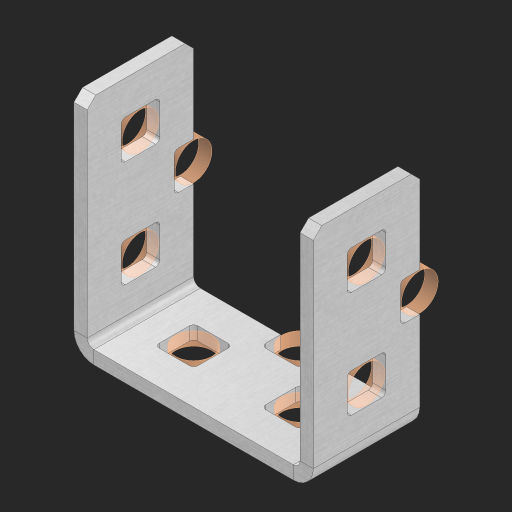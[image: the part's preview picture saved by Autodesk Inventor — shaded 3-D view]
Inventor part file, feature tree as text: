
AUTODESK INVENTOR PART (.ipt)
format: ipt  version: 2023 (Build 270158000, 158)  size: 576,512 bytes
history: native  units: in
note: dims shown in document units (in); Inventor stores cm internally (conversion verified against a paired STEP export)
features: other x90, extrude x82, sheet_metal_op x8, sketch x7, mirror x3, pattern_linear x2, chamfer x1
ambient origin geometry x8: Origin, YZ Plane, XZ Plane, XY Plane, X Axis, Y Axis, Z Axis, Center Point
bodies: Solid1 (feature_tree), Body (feature_tree)
feature tree (193):
  sheet_metal_op  "Flanges"
  sheet_metal_op  "Body Pattern"
  pattern_linear  "Center Pattern"  Spacing1=1.0in  [1 undecoded]
  other  "Arc Length"
  mirror  "Notch Mirror"
  pattern_linear  "Notch Pattern"  Spacing1=0.25in  [1 undecoded]
  other  "Diagonal Plane"
  mirror  "Flange 1"
  mirror  "Flange 2"
  chamfer  "End Chamfer"
  sketch  "Sketch1"  dims[d0=1.0in]
  other  "Plate1"
  sketch  "Sketch2"  dims[d1=0.5in]
  other  "Plate2"
  sheet_metal_op  "Bend1"
  sheet_metal_op  "Corner1"
  sketch  "Sketch8"  dims[d2=0.0625in]
  sketch  "Sketch9"  dims[d3=0.0625in]
  other  "Srf91"
  sheet_metal_op  "Body Pattern Sketch"
  other  "Srf92"
  sketch  "Sketch13"  dims[d4=0.0312in]
  sketch  "Sketch15"  dims[d5=0.125in]
  sketch  "Sketch16"  dims[d6=0.0625in d7=1.0in d8=90.0deg d9=0.0312in d10=0.25in d11=0.0625in d12=0.0625in d49=0.182in d50=0.02in d52=0.25in d53=0.0625in d54=0.0in d55=0.172in d56=1.0in d57=0.0in d60=0.3937in d62=0.5in d63=0.7874in d65=0.5in d85=0.1473in d86=0.1782in d88=0.04in d89=0.0625in d90=0.0in d91=0.04in d92=0.0491in d95=2.5in d96=0.04in d97=0.25in d98=45.0deg d99=0.25in d102=2.497in d106=0.182in d107=0.02in d108=0.5in d110=0.0625in d111=0.0in d112=0.172in d113=0.5in d114=0.0in d117=0.5in d118=0.5in d131=0.25in d132=0.25in]
  other  "Srf786"
  other  "Srf889"
  other  "Srf890"
  other  "Srf891"
  other  "Srf892"
  other  "Srf893"
  other  "Srf894"
  other  "Srf895"
  other  "Srf896"
  other  "Srf996"
  other  "Srf997"
  other  "Srf998"
  other  "Srf999"
  other  "Srf1000"
  other  "Srf1255"
  other  "Srf1256"
  other  "Srf1257"
  other  "Srf1258"
  other  "Srf1259"
  other  "Srf1315"
  other  "Srf1316"
  other  "Srf1317"
  other  "Srf1325"
  other  "Srf1326"
  other  "Srf1327"
  other  "Srf1328"
  other  "Srf1329"
  other  "Srf1330"
  other  "Srf1331"
  other  "Srf1332"
  other  "Srf1338"
  other  "Srf1339"
  other  "Srf1340"
  other  "Srf1341"
  other  "Srf1342"
  other  "Srf1369"
  other  "Srf1370"
  other  "Srf1371"
  other  "Srf1372"
  other  "Srf1373"
  other  "Srf1374"
  other  "Srf1375"
  other  "Srf1376"
  other  "Srf1384"
  other  "Srf1385"
  other  "Srf1386"
  other  "Srf1387"
  other  "Srf1388"
  other  "Srf1389"
  other  "Srf1390"
  other  "Srf1391"
  other  "Srf1397"
  other  "Srf1398"
  other  "Srf1399"
  other  "Srf1400"
  other  "Srf1401"
  other  "Srf1428"
  other  "Srf1429"
  other  "Srf1430"
  other  "Srf1431"
  other  "Srf1432"
  other  "Srf1433"
  other  "Srf1434"
  other  "Srf1473"
  other  "Srf1474"
  other  "Srf1475"
  other  "Srf1476"
  other  "Srf1477"
  other  "Srf1478"
  other  "Srf1479"
  other  "Srf1480"
  other  "Srf1481"
  other  "Srf1482"
  other  "Srf1483"
  other  "Srf1484"
  other  "Srf1485"
  other  "Srf1486"
  other  "Srf1487"
  other  "Srf1488"
  other  "Srf1489"
  other  "Srf1490"
  other  "Srf1491"
  sheet_metal_op  "Body Stamp"
  sheet_metal_op  "Body Circle"
  other  "Center Stamp"
  other  "Center Circle"
  sheet_metal_op  "Notch"
  extrude  "ExtrusionSrf92"  Depth=0.0625in
  extrude  "ExtrusionSrf889"  Depth=0.0625in
  extrude  "ExtrusionSrf890"  Depth=0.182in
  extrude  "ExtrusionSrf891"  Depth=0.02in
  extrude  "ExtrusionSrf892"  Depth=0.25in
  extrude  "ExtrusionSrf893"  Depth=0.0625in
  extrude  "ExtrusionSrf894"  TaperAngle=0.0deg  [1 undecoded]
  extrude  "ExtrusionSrf895"  Depth=0.25in
  extrude  "ExtrusionSrf896"  Depth=1.0in TaperAngle=0.0deg
  extrude  "ExtrusionSrf996"  Depth=0.3937in
  extrude  "ExtrusionSrf997"  Depth=0.5in
  extrude  "ExtrusionSrf998"  Depth=0.25in
  extrude  "ExtrusionSrf999"  Depth=0.25in
  extrude  "ExtrusionSrf1000"  Depth=0.25in
  extrude  "ExtrusionSrf1255"  Depth=0.0625in
  extrude  "ExtrusionSrf1256"  TaperAngle=0.0deg  [1 undecoded]
  extrude  "ExtrusionSrf1257"  Depth=0.25in
  extrude  "ExtrusionSrf1258"  Depth=0.25in
  extrude  "ExtrusionSrf1259"  Depth=0.25in
  extrude  "ExtrusionSrf1315"  Depth=0.25in TaperAngle=45.0deg
  extrude  "ExtrusionSrf1316"  Depth=0.25in
  extrude  "ExtrusionSrf1355"  Depth=0.25in
  extrude  "ExtrusionSrf1356"  Depth=0.182in
  extrude  "ExtrusionSrf1357"  Depth=0.02in
  extrude  "ExtrusionSrf1358"  Depth=0.5in
  extrude  "ExtrusionSrf1359"  Depth=0.0625in
  extrude  "ExtrusionSrf1360"  TaperAngle=0.0deg  [1 undecoded]
  extrude  "ExtrusionSrf1361"  Depth=0.25in
  extrude  "ExtrusionSrf1362"  Depth=0.5in TaperAngle=0.0deg
  extrude  "ExtrusionSrf1363"  Depth=0.5in
  extrude  "ExtrusionSrf1364"  Depth=0.5in
  extrude  "ExtrusionSrf1365"  Depth=0.25in
  extrude  "ExtrusionSrf1366"  Depth=0.25in
  extrude  "ExtrusionSrf1367"  [1 undecoded]
  extrude  "ExtrusionSrf1368"  [1 undecoded]
  extrude  "ExtrusionSrf1369"  [1 undecoded]
  extrude  "ExtrusionSrf1370"  [1 undecoded]
  extrude  "ExtrusionSrf1371"  [1 undecoded]
  extrude  "ExtrusionSrf1372"  [1 undecoded]
  extrude  "ExtrusionSrf1373"  [1 undecoded]
  extrude  "ExtrusionSrf1374"  [1 undecoded]
  extrude  "ExtrusionSrf1375"  [1 undecoded]
  extrude  "ExtrusionSrf1414"  [1 undecoded]
  extrude  "ExtrusionSrf1415"  [1 undecoded]
  extrude  "ExtrusionSrf1416"  [1 undecoded]
  extrude  "ExtrusionSrf1417"  [1 undecoded]
  extrude  "ExtrusionSrf1418"  [1 undecoded]
  extrude  "ExtrusionSrf1419"  [1 undecoded]
  extrude  "ExtrusionSrf1420"  [1 undecoded]
  extrude  "ExtrusionSrf1421"  [1 undecoded]
  extrude  "ExtrusionSrf1422"  [1 undecoded]
  extrude  "ExtrusionSrf1423"  [1 undecoded]
  extrude  "ExtrusionSrf1424"  [1 undecoded]
  extrude  "ExtrusionSrf1425"  [1 undecoded]
  extrude  "ExtrusionSrf1426"  [1 undecoded]
  extrude  "ExtrusionSrf1427"  [1 undecoded]
  extrude  "ExtrusionSrf1428"  [1 undecoded]
  extrude  "ExtrusionSrf1429"  [1 undecoded]
  extrude  "ExtrusionSrf1430"  [1 undecoded]
  extrude  "ExtrusionSrf1431"  [1 undecoded]
  extrude  "ExtrusionSrf1432"  [1 undecoded]
  extrude  "ExtrusionSrf1433"  [1 undecoded]
  extrude  "ExtrusionSrf1434"  [1 undecoded]
  extrude  "ExtrusionSrf1473"  [1 undecoded]
  extrude  "ExtrusionSrf1474"  [1 undecoded]
  extrude  "ExtrusionSrf1475"  [1 undecoded]
  extrude  "ExtrusionSrf1476"  [1 undecoded]
  extrude  "ExtrusionSrf1477"  [1 undecoded]
  extrude  "ExtrusionSrf1478"  [1 undecoded]
  extrude  "ExtrusionSrf1479"  [1 undecoded]
  extrude  "ExtrusionSrf1480"  [1 undecoded]
  extrude  "ExtrusionSrf1481"  [1 undecoded]
  extrude  "ExtrusionSrf1482"  [1 undecoded]
  extrude  "ExtrusionSrf1483"  [1 undecoded]
  extrude  "ExtrusionSrf1484"  [1 undecoded]
  extrude  "ExtrusionSrf1485"  [1 undecoded]
  extrude  "ExtrusionSrf1486"  [1 undecoded]
  extrude  "ExtrusionSrf1487"  [1 undecoded]
  extrude  "ExtrusionSrf1488"  [1 undecoded]
  extrude  "ExtrusionSrf1489"  [1 undecoded]
  extrude  "ExtrusionSrf1490"  [1 undecoded]
  extrude  "ExtrusionSrf1491"  [1 undecoded]
note: 54 required parameter values undecoded (feature->parameter linkage not recoverable at this tier; creation-order binding heuristic only, values carry confidence <= 0.55)
